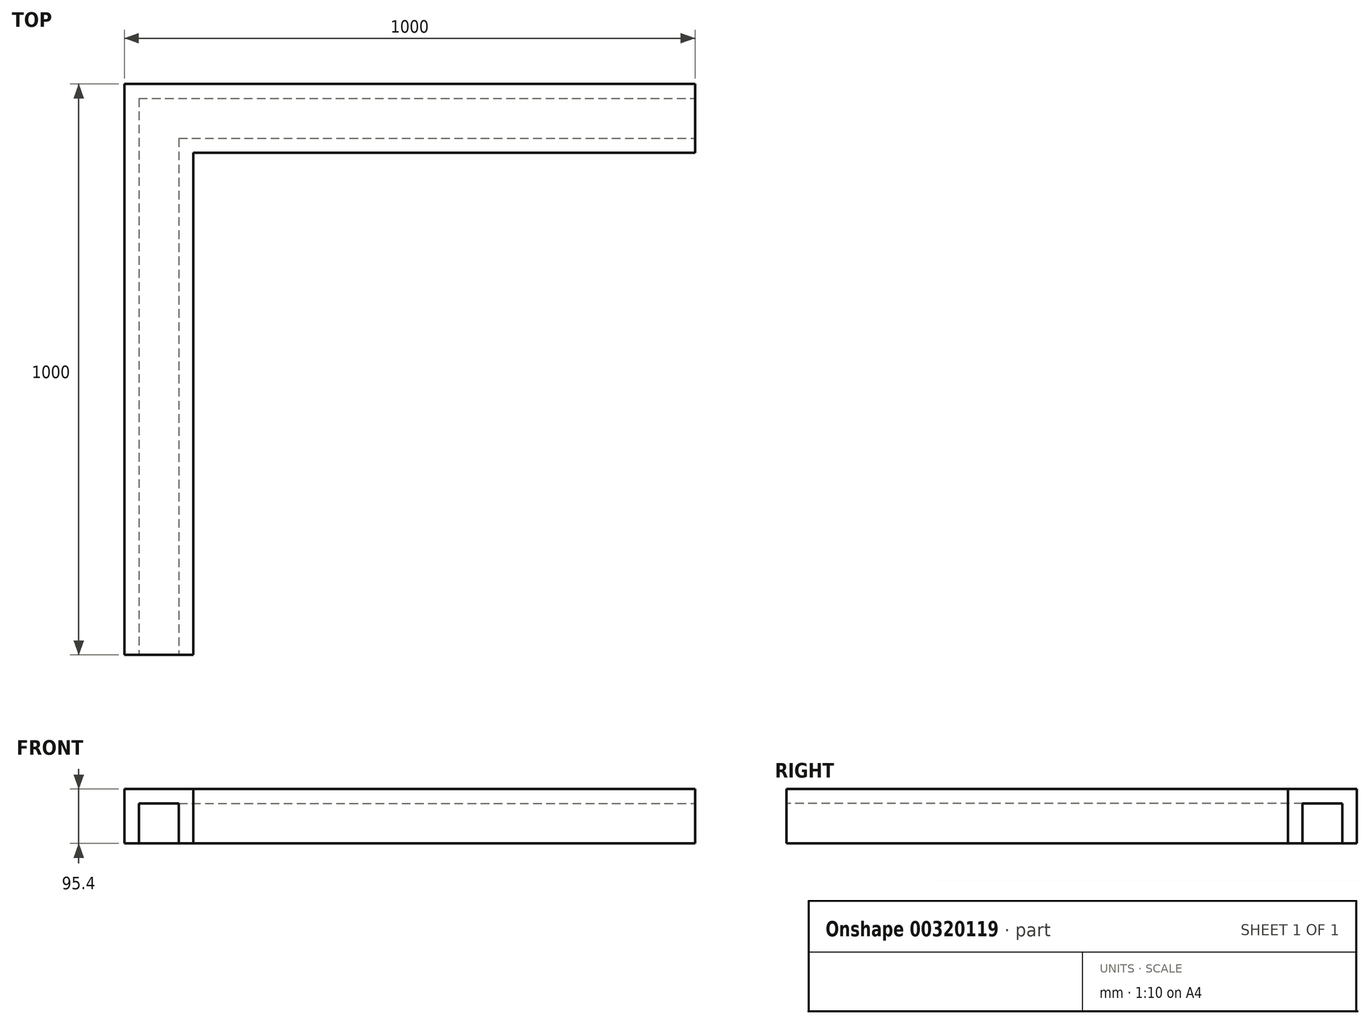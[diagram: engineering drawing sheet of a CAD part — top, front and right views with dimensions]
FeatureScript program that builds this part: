
annotation { "Feature Type Name" : "Feature", "Feature Type Description" : "" }
export const myFeature = defineFeature(function(context is Context, id is Id, definition is map)
    precondition{}
    {
        {
            var Q0;
            Q0=qCreatedBy(makeId("Top.planeOp"),FACE);
            var sketch = newSketch(context, id + "F0", { "sketchPlane" : qUnion([Q0])});
            skLineSegment(sketch, "E0.bottom", {"start": v(-176.89, 103.34) * mm, "end": v(-106.89, 103.34) * mm});
            skLineSegment(sketch, "E0.top", {"start": v(-176.89, -871.26) * mm, "end": v(-106.89, -871.26) * mm});
            skLineSegment(sketch, "E0.left", {"start": v(-176.89, 103.34) * mm, "end": v(-176.89, -871.26) * mm});
            skLineSegment(sketch, "E0.right", {"start": v(-106.89, 33.34) * mm, "end": v(-106.89, -871.26) * mm});
            skLineSegment(sketch, "E1.bottom", {"start": v(-176.89, 103.34) * mm, "end": v(797.71, 103.34) * mm});
            skLineSegment(sketch, "E1.top", {"start": v(-106.89, 33.34) * mm, "end": v(797.71, 33.34) * mm});
            skLineSegment(sketch, "E1.left", {"start": v(-176.89, 103.34) * mm, "end": v(-176.89, 33.34) * mm});
            skLineSegment(sketch, "E1.right", {"start": v(797.71, 103.34) * mm, "end": v(797.71, 33.34) * mm});
            skLineSegment(sketch, "E2.bottom", {"start": v(-202.29, 128.74) * mm, "end": v(797.71, 128.74) * mm});
            skLineSegment(sketch, "E2.left", {"start": v(-202.29, 128.74) * mm, "end": v(-202.29, -1.54) * mm});
            skLineSegment(sketch, "E2.right", {"start": v(797.71, 128.74) * mm, "end": v(797.71, 7.94) * mm});
            skLineSegment(sketch, "E3.bottom", {"start": v(-202.29, 128.74) * mm, "end": v(-81.49, 128.74) * mm});
            skLineSegment(sketch, "E3.top", {"start": v(-202.29, -871.26) * mm, "end": v(-81.49, -871.26) * mm});
            skLineSegment(sketch, "E3.left", {"start": v(-202.29, 128.74) * mm, "end": v(-202.29, -871.26) * mm});
            skLineSegment(sketch, "E3.right", {"start": v(-81.49, 7.94) * mm, "end": v(-81.49, -871.26) * mm});
            skLineSegment(sketch, "E4.trimOffspring", {"start": v(-81.49, 7.94) * mm, "end": v(797.71, 7.94) * mm});
            skSolve(sketch);
        }
        {
            var Q0;
            {var subQ9=sQuery(id+"F0.wireOp",EDGE,"E0.left");Q0=makeQuery(id+"F0.imprint","IMPRINT",FACE,{"disambiguationData":[TD([[makeQuery(id+"F0.imprint","IMPRINT",EDGE,{"derivedFrom":subQ9}),-1.0]])]});}
            var Q1;
            {var subQ7=sQuery(id+"F0.wireOp",EDGE,"E0.left");Q1=makeQuery(id+"F0.imprint","IMPRINT",FACE,{"disambiguationData":[TD([[makeQuery(id+"F0.imprint","IMPRINT",EDGE,{"derivedFrom":subQ7}),1.0]])]});}
            var Q2;
            {var subQ1=sQuery(id+"F0.wireOp",EDGE,"E0.right");Q2=makeQuery(id+"F0.imprint","IMPRINT",FACE,{"disambiguationData":[TD([[makeQuery(id+"F0.imprint","IMPRINT",EDGE,{"derivedFrom":subQ1}),1.0]])]});}
            extrude(context, id + "F1", {"entities" : qUnion([Q0, Q1, Q2]), "depth" : 70 * mm + 25.4 * mm});
        }
        {
            var Q0;
            {var subQ7=sQuery(id+"F0.wireOp",EDGE,"E0.left");Q0=makeQuery(id+"F0.imprint","IMPRINT",FACE,{"disambiguationData":[TD([[makeQuery(id+"F0.imprint","IMPRINT",EDGE,{"derivedFrom":subQ7}),1.0]])]});}
            extrude(context, id + "F2", {"entities" : qUnion([Q0]), "operationType" : NewBodyOperationType.REMOVE, "depth" : 70 * mm});
        }
    });
